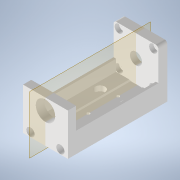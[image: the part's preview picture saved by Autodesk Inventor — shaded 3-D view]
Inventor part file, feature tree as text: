
AUTODESK INVENTOR PART (.ipt)
format: ipt  version: 2022 (Build 260153000, 153)  size: 242,688 bytes
history: mixed  units: mm
features: imported_body x4, extrude x3, sketch x3, projected_geometry x3, plane x1
ambient origin geometry x8: Origin, YZ Plane, XZ Plane, XY Plane, X Axis, Y Axis, Z Axis, Center Point
bodies: Volumenkörper1 (imported_parasolid), Volumenkörper2 (imported_parasolid), Volumenkörper3 (imported_parasolid)
feature tree (14):
  extrude  "Extrusion1"  Depth=61.0mm
  extrude  "Extrusion2"  Depth=5.5mm TaperAngle=0.0deg
  extrude  "Extrusion3"  [1 undecoded]
  plane  "Arbeitsebene1"
  sketch  "Skizze1"  dims[d0=0.0mm d1=61.0mm]
  projected_geometry  "Projizierte Kontur1"
  sketch  "Skizze2"  dims[d2=0.0mm d3=0.0mm d4=5.5mm d5=0.0mm]
  projected_geometry  "Projizierte Kontur2"
  sketch  "Skizze3"  dims[d6=0.0mm d7=0.0mm]
  projected_geometry  "Projizierte Kontur3"
  imported_body  "Basis1"
  imported_body  "Basis2"
  imported_body  "Basis3"
  imported_body  NMx_Import_Brep_tag  [imported B-rep: ~69 faces, bbox_mm=[30.0, 35.0, 72.5]]
note: 1 required parameter value undecoded (feature->parameter linkage not recoverable at this tier; creation-order binding heuristic only, values carry confidence <= 0.55)
